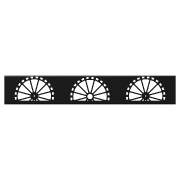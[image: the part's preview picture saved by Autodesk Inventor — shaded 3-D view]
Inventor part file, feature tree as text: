
AUTODESK INVENTOR PART (.ipt)
format: ipt  version: 2015 (Build 190159000, 159)  size: 1,014,272 bytes
history: native  units: in
note: dims shown in document units (in); Inventor stores cm internally (conversion verified against a paired STEP export)
features: other x4, sketch x4, extrude x2, sheet_metal_op x2, hole x1, fillet x1, imported_body x1
ambient origin geometry x8: Origin, YZ Plane, XZ Plane, XY Plane, X Axis, Y Axis, Z Axis, Center Point
bodies: Body1 (feature_tree)
feature tree (15):
  other  "PartBody"
  other  "Part21"
  extrude  "Extrusion1"  Depth=0.09in
  extrude  "Extrusion2"  Depth=0.09in
  sheet_metal_op  "Flange1"
  hole  "Hole1"  [1 undecoded]
  fillet  "Fillet1"  Radius=0.09in
  imported_body  "Base1"
  sketch  "Sketch1"  dims[d0=0.09in d1=0.045in]
  other  "Plate1"
  sheet_metal_op  "Bend1"
  sketch  "Sketch2"  dims[d2=0.18in d3=0.09in]
  sketch  "Sketch3"  dims[d4=1.18in d5=90.0deg d6=0.09in d7=0.36in d8=0.09in]
  sketch  "Sketch4"  dims[d9=0.09in d19=0.266in d20=0.75in d21=0.375in d22=0.25in d23=0.5635in d24=0.09in d25=0.8108in d26=0.375in d27=1.0in d28=0.0in d29=0.375in d30=1.0in d31=0.0in d32=0.5in d33=0.5in d34=14.1732in d36=1.0in d37=0.3937in d39=1.0in d41=0.125in]
  other  "Definition1"
note: 1 required parameter value undecoded (feature->parameter linkage not recoverable at this tier; creation-order binding heuristic only, values carry confidence <= 0.55)
